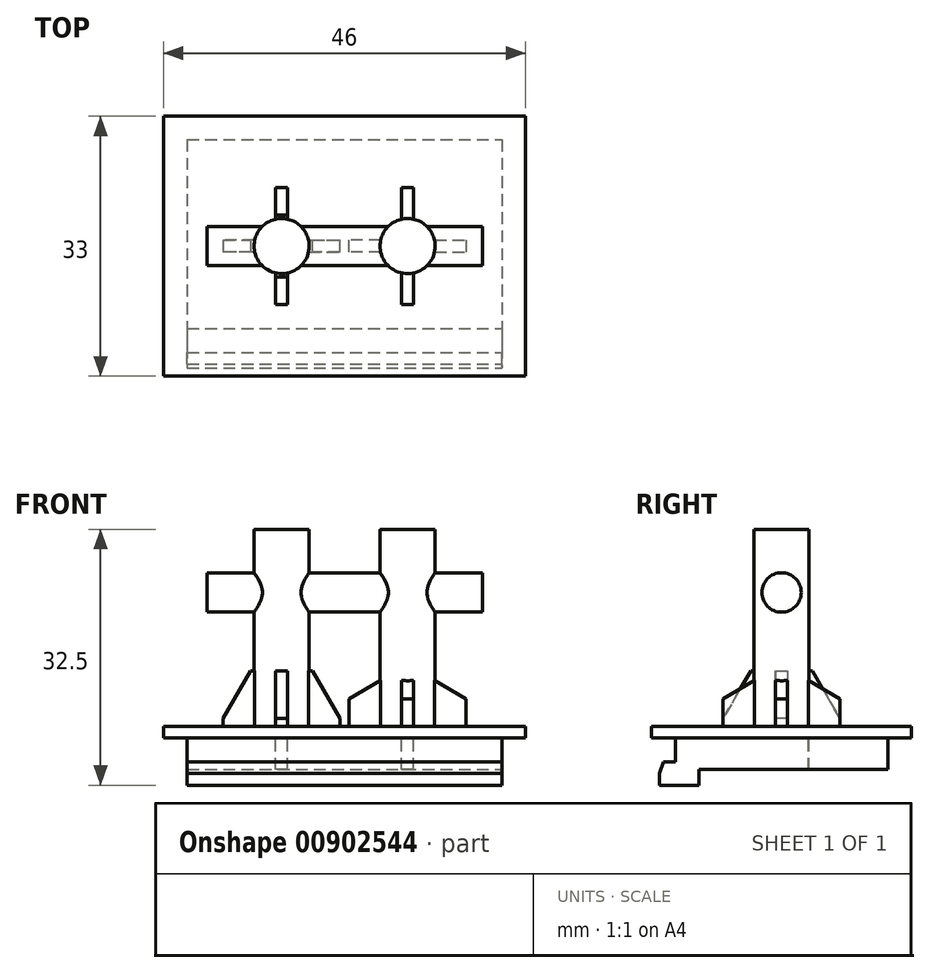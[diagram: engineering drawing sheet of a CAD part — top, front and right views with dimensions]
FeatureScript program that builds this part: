
annotation { "Feature Type Name" : "Feature", "Feature Type Description" : "" }
export const myFeature = defineFeature(function(context is Context, id is Id, definition is map)
    precondition{}
    {
        {
            var Q0;
            Q0=qCreatedBy(makeId("Top.planeOp"),FACE);
            var sketch = newSketch(context, id + "F0", { "sketchPlane" : qUnion([Q0])});
            skLineSegment(sketch, "E0.bottom", {"start": v(-20, 13.5) * mm, "end": v(20, 13.5) * mm});
            skLineSegment(sketch, "E0.top", {"start": v(-20, -13.5) * mm, "end": v(20, -13.5) * mm});
            skLineSegment(sketch, "E0.left", {"start": v(-20, 13.5) * mm, "end": v(-20, -13.5) * mm});
            skLineSegment(sketch, "E0.right", {"start": v(20, 13.5) * mm, "end": v(20, -13.5) * mm});
            skPoint(sketch, "E0.middle", {"position": v(0, 0) * mm});
            skLineSegment(sketch, "E1.bottom", {"start": v(-23, 16.5) * mm, "end": v(23, 16.5) * mm});
            skLineSegment(sketch, "E1.top", {"start": v(-23, -16.5) * mm, "end": v(23, -16.5) * mm});
            skLineSegment(sketch, "E1.left", {"start": v(-23, 16.5) * mm, "end": v(-23, -16.5) * mm});
            skLineSegment(sketch, "E1.right", {"start": v(23, 16.5) * mm, "end": v(23, -16.5) * mm});
            skLineSegment(sketch, "E2", {"start": v(0, 0) * mm, "end": v(-8, 0) * mm});
            skLineSegment(sketch, "E3", {"start": v(0, 0) * mm, "end": v(8, 0) * mm});
            skCircle(sketch, "E4", {"center": v(-8, 0) * mm, "radius": 3.5 * mm});
            skCircle(sketch, "E5", {"center": v(8, 0) * mm, "radius": 3.5 * mm});
            skLineSegment(sketch, "E6.bottom", {"start": v(-7.25, 3.42) * mm, "end": v(-8.75, 3.42) * mm});
            skLineSegment(sketch, "E6.top", {"start": v(-7.25, 7.42) * mm, "end": v(-8.75, 7.42) * mm});
            skLineSegment(sketch, "E6.left", {"start": v(-7.25, 3.42) * mm, "end": v(-7.25, 7.42) * mm});
            skLineSegment(sketch, "E6.right", {"start": v(-8.75, 3.42) * mm, "end": v(-8.75, 7.42) * mm});
            skPoint(sketch, "E6.middle", {"position": v(-8, 5.42) * mm});
            skLineSegment(sketch, "E7.bottom", {"start": v(7.25, 3.42) * mm, "end": v(8.75, 3.42) * mm});
            skLineSegment(sketch, "E7.top", {"start": v(7.25, 7.42) * mm, "end": v(8.75, 7.42) * mm});
            skLineSegment(sketch, "E7.left", {"start": v(7.25, 3.42) * mm, "end": v(7.25, 7.42) * mm});
            skLineSegment(sketch, "E7.right", {"start": v(8.75, 3.42) * mm, "end": v(8.75, 7.42) * mm});
            skPoint(sketch, "E7.middle", {"position": v(8, 5.42) * mm});
            skLineSegment(sketch, "E8.1.0", {"start": v(-11.42, -0.75) * mm, "end": v(-15.42, -0.75) * mm});
            skLineSegment(sketch, "E8.1.1", {"start": v(-15.42, 0.75) * mm, "end": v(-15.42, -0.75) * mm});
            skLineSegment(sketch, "E8.1.2", {"start": v(-11.42, 0.75) * mm, "end": v(-15.42, 0.75) * mm});
            skLineSegment(sketch, "E8.2.0", {"start": v(-7.25, -3.42) * mm, "end": v(-7.25, -7.42) * mm});
            skLineSegment(sketch, "E8.2.1", {"start": v(-8.75, -7.42) * mm, "end": v(-7.25, -7.42) * mm});
            skLineSegment(sketch, "E8.2.2", {"start": v(-8.75, -3.42) * mm, "end": v(-8.75, -7.42) * mm});
            skLineSegment(sketch, "E8.3.0", {"start": v(-4.58, 0.75) * mm, "end": v(-0.58, 0.75) * mm});
            skLineSegment(sketch, "E8.3.1", {"start": v(-0.58, -0.75) * mm, "end": v(-0.58, 0.75) * mm});
            skLineSegment(sketch, "E8.3.2", {"start": v(-4.58, -0.75) * mm, "end": v(-0.58, -0.75) * mm});
            skLineSegment(sketch, "E9.1.0", {"start": v(0.58, -0.75) * mm, "end": v(0.58, 0.75) * mm});
            skLineSegment(sketch, "E9.1.1", {"start": v(4.58, 0.75) * mm, "end": v(0.58, 0.75) * mm});
            skLineSegment(sketch, "E9.1.2", {"start": v(4.58, -0.75) * mm, "end": v(0.58, -0.75) * mm});
            skLineSegment(sketch, "E9.2.0", {"start": v(8.75, -7.42) * mm, "end": v(7.25, -7.42) * mm});
            skLineSegment(sketch, "E9.2.1", {"start": v(7.25, -3.42) * mm, "end": v(7.25, -7.42) * mm});
            skLineSegment(sketch, "E9.2.2", {"start": v(8.75, -3.42) * mm, "end": v(8.75, -7.42) * mm});
            skLineSegment(sketch, "E9.3.0", {"start": v(15.42, 0.75) * mm, "end": v(15.42, -0.75) * mm});
            skLineSegment(sketch, "E9.3.1", {"start": v(11.42, -0.75) * mm, "end": v(15.42, -0.75) * mm});
            skLineSegment(sketch, "E9.3.2", {"start": v(11.42, 0.75) * mm, "end": v(15.42, 0.75) * mm});
            skSolve(sketch);
        }
        {
            var Q0;
            Q0 = qSketchRegion(id + "F0", true);
            var Q1;
            Q1=makeQuery(id+"F0.imprint","IMPRINT",FACE,{"disambiguationData":[TD([[makeQuery(id+"F0.imprint","IMPRINT",EDGE,{"derivedFrom":sQuery(id+"F0.wireOp",EDGE,"E0.bottom")}),-1.0]])]});
            var Q2;
            Q2=makeQuery(id+"F0.imprint","IMPRINT",FACE,{"disambiguationData":[TD([[makeQuery(id+"F0.imprint","IMPRINT",EDGE,{"derivedFrom":sQuery(id+"F0.wireOp",EDGE,"E4")}),1.0]])]});
            var Q3;
            Q3=makeQuery(id+"F0.imprint","IMPRINT",FACE,{"disambiguationData":[TD([[makeQuery(id+"F0.imprint","IMPRINT",EDGE,{"derivedFrom":sQuery(id+"F0.wireOp",EDGE,"E5")}),1.0]])]});
            var Q4;
            {var subQ0=sQuery(id+"F0.wireOp",EDGE,"E8.2.0");Q4=makeQuery(id+"F0.imprint","IMPRINT",FACE,{"disambiguationData":[TD([[makeQuery(id+"F0.imprint","IMPRINT",EDGE,{"derivedFrom":subQ0}),-1.0]])]});}
            var Q5;
            Q5=makeQuery(id+"F0.imprint","IMPRINT",FACE,{"disambiguationData":[TD([[makeQuery(id+"F0.imprint","IMPRINT",EDGE,{"derivedFrom":sQuery(id+"F0.wireOp",EDGE,"E6.top")}),1.0]])]});
            var Q6;
            {var subQ0=sQuery(id+"F0.wireOp",EDGE,"E8.1.0");Q6=makeQuery(id+"F0.imprint","IMPRINT",FACE,{"disambiguationData":[TD([[makeQuery(id+"F0.imprint","IMPRINT",EDGE,{"derivedFrom":subQ0}),-1.0]])]});}
            var Q7;
            {var subQ5=sQuery(id+"F0.wireOp",EDGE,"E8.3.0");Q7=makeQuery(id+"F0.imprint","IMPRINT",FACE,{"disambiguationData":[TD([[makeQuery(id+"F0.imprint","IMPRINT",EDGE,{"derivedFrom":subQ5}),-1.0]])]});}
            var Q8;
            {var subQ5=sQuery(id+"F0.wireOp",EDGE,"E8.3.2");Q8=makeQuery(id+"F0.imprint","IMPRINT",FACE,{"disambiguationData":[TD([[makeQuery(id+"F0.imprint","IMPRINT",EDGE,{"derivedFrom":subQ5}),1.0]])]});}
            var Q9;
            {var subQ5=sQuery(id+"F0.wireOp",EDGE,"E9.1.2");Q9=makeQuery(id+"F0.imprint","IMPRINT",FACE,{"disambiguationData":[TD([[makeQuery(id+"F0.imprint","IMPRINT",EDGE,{"derivedFrom":subQ5}),-1.0]])]});}
            var Q10;
            {var subQ5=sQuery(id+"F0.wireOp",EDGE,"E9.1.1");Q10=makeQuery(id+"F0.imprint","IMPRINT",FACE,{"disambiguationData":[TD([[makeQuery(id+"F0.imprint","IMPRINT",EDGE,{"derivedFrom":subQ5}),1.0]])]});}
            var Q11;
            Q11=makeQuery(id+"F0.imprint","IMPRINT",FACE,{"disambiguationData":[TD([[makeQuery(id+"F0.imprint","IMPRINT",EDGE,{"derivedFrom":sQuery(id+"F0.wireOp",EDGE,"E7.top")}),-1.0]])]});
            var Q12;
            Q12=makeQuery(id+"F0.imprint","IMPRINT",FACE,{"disambiguationData":[TD([[makeQuery(id+"F0.imprint","IMPRINT",EDGE,{"derivedFrom":sQuery(id+"F0.wireOp",EDGE,"E9.3.0")}),-1.0]])]});
            var Q13;
            Q13=makeQuery(id+"F0.imprint","IMPRINT",FACE,{"disambiguationData":[TD([[makeQuery(id+"F0.imprint","IMPRINT",EDGE,{"derivedFrom":sQuery(id+"F0.wireOp",EDGE,"E9.2.0")}),-1.0]])]});
            var Q14;
            {var subQ0=sQuery(id+"F0.wireOp",EDGE,"E7.bottom");Q14=makeQuery(id+"F0.imprint","IMPRINT",FACE,{"disambiguationData":[TD([[makeQuery(id+"F0.imprint","IMPRINT",EDGE,{"derivedFrom":subQ0}),1.0]])]});}
            var Q15;
            {var subQ0=sQuery(id+"F0.wireOp",EDGE,"E6.bottom");Q15=makeQuery(id+"F0.imprint","IMPRINT",FACE,{"disambiguationData":[TD([[makeQuery(id+"F0.imprint","IMPRINT",EDGE,{"derivedFrom":subQ0}),-1.0]])]});}
            extrude(context, id + "F1", {"entities" : qUnion([Q0, Q1, Q2, Q3, Q4, Q5, Q6, Q7, Q8, Q9, Q10, Q11, Q12, Q13, Q14, Q15]), "oppositeDirection" : true, "depth" : 1.5 * mm, "offsetDistance" : 25 * mm});
        }
        {
            var Q0;
            {var subQ0=sQuery(id+"F0.wireOp",EDGE,"E8.2.0");Q0=makeQuery(id+"F0.imprint","IMPRINT",FACE,{"disambiguationData":[TD([[makeQuery(id+"F0.imprint","IMPRINT",EDGE,{"derivedFrom":subQ0}),-1.0]])]});}
            var Q1;
            {var subQ0=sQuery(id+"F0.wireOp",EDGE,"E8.1.0");Q1=makeQuery(id+"F0.imprint","IMPRINT",FACE,{"disambiguationData":[TD([[makeQuery(id+"F0.imprint","IMPRINT",EDGE,{"derivedFrom":subQ0}),-1.0]])]});}
            var Q2;
            Q2=makeQuery(id+"F0.imprint","IMPRINT",FACE,{"disambiguationData":[TD([[makeQuery(id+"F0.imprint","IMPRINT",EDGE,{"derivedFrom":sQuery(id+"F0.wireOp",EDGE,"E6.top")}),1.0]])]});
            var Q3;
            {var subQ5=sQuery(id+"F0.wireOp",EDGE,"E9.1.2");Q3=makeQuery(id+"F0.imprint","IMPRINT",FACE,{"disambiguationData":[TD([[makeQuery(id+"F0.imprint","IMPRINT",EDGE,{"derivedFrom":subQ5}),-1.0]])]});}
            var Q4;
            {var subQ5=sQuery(id+"F0.wireOp",EDGE,"E9.1.1");Q4=makeQuery(id+"F0.imprint","IMPRINT",FACE,{"disambiguationData":[TD([[makeQuery(id+"F0.imprint","IMPRINT",EDGE,{"derivedFrom":subQ5}),1.0]])]});}
            var Q5;
            {var subQ5=sQuery(id+"F0.wireOp",EDGE,"E8.3.2");Q5=makeQuery(id+"F0.imprint","IMPRINT",FACE,{"disambiguationData":[TD([[makeQuery(id+"F0.imprint","IMPRINT",EDGE,{"derivedFrom":subQ5}),1.0]])]});}
            var Q6;
            {var subQ5=sQuery(id+"F0.wireOp",EDGE,"E8.3.0");Q6=makeQuery(id+"F0.imprint","IMPRINT",FACE,{"disambiguationData":[TD([[makeQuery(id+"F0.imprint","IMPRINT",EDGE,{"derivedFrom":subQ5}),-1.0]])]});}
            var Q7;
            Q7=makeQuery(id+"F0.imprint","IMPRINT",FACE,{"disambiguationData":[TD([[makeQuery(id+"F0.imprint","IMPRINT",EDGE,{"derivedFrom":sQuery(id+"F0.wireOp",EDGE,"E7.top")}),-1.0]])]});
            var Q8;
            Q8=makeQuery(id+"F0.imprint","IMPRINT",FACE,{"disambiguationData":[TD([[makeQuery(id+"F0.imprint","IMPRINT",EDGE,{"derivedFrom":sQuery(id+"F0.wireOp",EDGE,"E9.3.0")}),-1.0]])]});
            var Q9;
            Q9=makeQuery(id+"F0.imprint","IMPRINT",FACE,{"disambiguationData":[TD([[makeQuery(id+"F0.imprint","IMPRINT",EDGE,{"derivedFrom":sQuery(id+"F0.wireOp",EDGE,"E9.2.0")}),-1.0]])]});
            var Q10;
            Q10=makeQuery(id+"F0.imprint","IMPRINT",FACE,{"disambiguationData":[TD([[makeQuery(id+"F0.imprint","IMPRINT",EDGE,{"derivedFrom":sQuery(id+"F0.wireOp",EDGE,"E0.bottom")}),-1.0]])]});
            var Q11;
            {var subQ3=sQuery(id+"F0.wireOp",EDGE,"E6.bottom");Q11=makeQuery(id+"F0.imprint","IMPRINT",FACE,{"disambiguationData":[TD([[makeQuery(id+"F0.imprint","IMPRINT",EDGE,{"derivedFrom":subQ3}),1.0]])]});}
            var Q12;
            {var subQ4=sQuery(id+"F0.wireOp",EDGE,"E7.bottom");Q12=makeQuery(id+"F0.imprint","IMPRINT",FACE,{"disambiguationData":[TD([[makeQuery(id+"F0.imprint","IMPRINT",EDGE,{"derivedFrom":subQ4}),-1.0]])]});}
            extrude(context, id + "F2", {"entities" : qUnion([Q0, Q1, Q2, Q3, Q4, Q5, Q6, Q7, Q8, Q9, Q10, Q11, Q12]), "operationType" : NewBodyOperationType.ADD, "oppositeDirection" : true, "depth" : 5.5 * mm, "offsetDistance" : 25 * mm});
        }
        {
            var Q0;
            Q0=makeQuery(id+"F0.imprint","IMPRINT",FACE,{"disambiguationData":[TD([[makeQuery(id+"F0.imprint","IMPRINT",EDGE,{"derivedFrom":sQuery(id+"F0.wireOp",EDGE,"E4")}),1.0]])]});
            var Q1;
            Q1=makeQuery(id+"F0.imprint","IMPRINT",FACE,{"disambiguationData":[TD([[makeQuery(id+"F0.imprint","IMPRINT",EDGE,{"derivedFrom":sQuery(id+"F0.wireOp",EDGE,"E5")}),1.0]])]});
            var Q2;
            {var subQ0=sQuery(id+"F0.wireOp",EDGE,"E6.bottom");Q2=makeQuery(id+"F0.imprint","IMPRINT",FACE,{"disambiguationData":[TD([[makeQuery(id+"F0.imprint","IMPRINT",EDGE,{"derivedFrom":subQ0}),-1.0]])]});}
            var Q3;
            {var subQ0=sQuery(id+"F0.wireOp",EDGE,"E7.bottom");Q3=makeQuery(id+"F0.imprint","IMPRINT",FACE,{"disambiguationData":[TD([[makeQuery(id+"F0.imprint","IMPRINT",EDGE,{"derivedFrom":subQ0}),1.0]])]});}
            extrude(context, id + "F3", {"entities" : qUnion([Q0, Q1, Q2, Q3]), "operationType" : NewBodyOperationType.ADD, "depth" : 25 * mm, "offsetDistance" : 25 * mm});
        }
        {
            var Q0;
            Q0=qCreatedBy(makeId("Right.planeOp"),FACE);
            var sketch = newSketch(context, id + "F4", { "sketchPlane" : qUnion([Q0])});
            skCircle(sketch, "E10", {"center": v(0, 17) * mm, "radius": 2.5 * mm});
            skSolve(sketch);
        }
        {
            var Q0;
            Q0=makeQuery(id+"F4.imprint","IMPRINT",FACE,{"disambiguationData":[TD([[makeQuery(id+"F4.imprint","IMPRINT",EDGE,{"derivedFrom":sQuery(id+"F4.wireOp",EDGE,"E10")}),1.0]])]});
            extrude(context, id + "F5", {"entities" : qUnion([Q0]), "operationType" : NewBodyOperationType.ADD, "depth" : 35 * mm, "offsetDistance" : 25 * mm, "symmetric" : true});
        }
        {
            var Q0;
            Q0=makeQuery(id+"F0.imprint","IMPRINT",FACE,{"disambiguationData":[TD([[makeQuery(id+"F0.imprint","IMPRINT",EDGE,{"derivedFrom":sQuery(id+"F0.wireOp",EDGE,"E6.top")}),1.0]])]});
            var Q1;
            {var subQ0=sQuery(id+"F0.wireOp",EDGE,"E8.2.0");Q1=makeQuery(id+"F0.imprint","IMPRINT",FACE,{"disambiguationData":[TD([[makeQuery(id+"F0.imprint","IMPRINT",EDGE,{"derivedFrom":subQ0}),-1.0]])]});}
            var Q2;
            {var subQ0=sQuery(id+"F0.wireOp",EDGE,"E8.1.0");Q2=makeQuery(id+"F0.imprint","IMPRINT",FACE,{"disambiguationData":[TD([[makeQuery(id+"F0.imprint","IMPRINT",EDGE,{"derivedFrom":subQ0}),-1.0]])]});}
            var Q3;
            {var subQ5=sQuery(id+"F0.wireOp",EDGE,"E8.3.2");Q3=makeQuery(id+"F0.imprint","IMPRINT",FACE,{"disambiguationData":[TD([[makeQuery(id+"F0.imprint","IMPRINT",EDGE,{"derivedFrom":subQ5}),1.0]])]});}
            var Q4;
            {var subQ5=sQuery(id+"F0.wireOp",EDGE,"E9.1.2");Q4=makeQuery(id+"F0.imprint","IMPRINT",FACE,{"disambiguationData":[TD([[makeQuery(id+"F0.imprint","IMPRINT",EDGE,{"derivedFrom":subQ5}),-1.0]])]});}
            var Q5;
            Q5=makeQuery(id+"F0.imprint","IMPRINT",FACE,{"disambiguationData":[TD([[makeQuery(id+"F0.imprint","IMPRINT",EDGE,{"derivedFrom":sQuery(id+"F0.wireOp",EDGE,"E9.2.0")}),-1.0]])]});
            var Q6;
            Q6=makeQuery(id+"F0.imprint","IMPRINT",FACE,{"disambiguationData":[TD([[makeQuery(id+"F0.imprint","IMPRINT",EDGE,{"derivedFrom":sQuery(id+"F0.wireOp",EDGE,"E9.3.0")}),-1.0]])]});
            var Q7;
            Q7=makeQuery(id+"F0.imprint","IMPRINT",FACE,{"disambiguationData":[TD([[makeQuery(id+"F0.imprint","IMPRINT",EDGE,{"derivedFrom":sQuery(id+"F0.wireOp",EDGE,"E7.top")}),-1.0]])]});
            var Q8;
            {var subQ5=sQuery(id+"F0.wireOp",EDGE,"E8.3.0");Q8=makeQuery(id+"F0.imprint","IMPRINT",FACE,{"disambiguationData":[TD([[makeQuery(id+"F0.imprint","IMPRINT",EDGE,{"derivedFrom":subQ5}),-1.0]])]});}
            var Q9;
            {var subQ5=sQuery(id+"F0.wireOp",EDGE,"E9.1.1");Q9=makeQuery(id+"F0.imprint","IMPRINT",FACE,{"disambiguationData":[TD([[makeQuery(id+"F0.imprint","IMPRINT",EDGE,{"derivedFrom":subQ5}),1.0]])]});}
            extrude(context, id + "F6", {"entities" : qUnion([Q0, Q1, Q2, Q3, Q4, Q5, Q6, Q7, Q8, Q9]), "operationType" : NewBodyOperationType.ADD, "depth" : 7 * mm, "offsetDistance" : 25 * mm});
        }
        {
            var Q0;
            Q0=makeQuery(id+"F6.opExtrude","CAP_EDGE",EDGE,{"disambiguationData":[OSD([sQuery(id+"F0.wireOp",EDGE,"E8.2.1")])],"isStart":false});
            var Q1;
            Q1=makeQuery(id+"F6.opExtrude","CAP_EDGE",EDGE,{"disambiguationData":[OSD([sQuery(id+"F0.wireOp",EDGE,"E8.3.1")])],"isStart":false});
            var Q2;
            Q2=makeQuery(id+"F6.opExtrude","CAP_EDGE",EDGE,{"disambiguationData":[OSD([sQuery(id+"F0.wireOp",EDGE,"E6.top")])],"isStart":false});
            var Q3;
            Q3=makeQuery(id+"F6.opExtrude","CAP_EDGE",EDGE,{"disambiguationData":[OSD([sQuery(id+"F0.wireOp",EDGE,"E8.1.1")])],"isStart":false});
            chamfer(context, id + "F7", {"entities" : qUnion([Q0, Q1, Q2, Q3]), "chamferType" : ChamferType.TWO_OFFSETS, "width1" : 3.5 * mm, "oppositeDirection" : false, "width2" : 6 * mm, "tangentPropagation" : true});
        }
        {
            var Q0;
            Q0=makeQuery(id+"F6.opExtrude","CAP_EDGE",EDGE,{"disambiguationData":[OSD([sQuery(id+"F0.wireOp",EDGE,"E9.1.0")])],"isStart":false});
            var Q1;
            Q1=makeQuery(id+"F6.opExtrude","CAP_EDGE",EDGE,{"disambiguationData":[OSD([sQuery(id+"F0.wireOp",EDGE,"E9.2.0")])],"isStart":false});
            var Q2;
            Q2=makeQuery(id+"F6.opExtrude","CAP_EDGE",EDGE,{"disambiguationData":[OSD([sQuery(id+"F0.wireOp",EDGE,"E9.3.0")])],"isStart":false});
            var Q3;
            Q3=makeQuery(id+"F6.opExtrude","CAP_EDGE",EDGE,{"disambiguationData":[OSD([sQuery(id+"F0.wireOp",EDGE,"E7.top")])],"isStart":false});
            chamfer(context, id + "F8", {"entities" : qUnion([Q0, Q1, Q2, Q3]), "chamferType" : ChamferType.TWO_OFFSETS, "width1" : 6 * mm, "oppositeDirection" : false, "width2" : 3.5 * mm, "tangentPropagation" : true});
        }
        {
            var Q0;
            Q0=makeQuery(id+"F2.opExtrude","CAP_FACE",FACE,{"disambiguationData":[OSD([sQuery(id+"F0.wireOp",EDGE,"E0.bottom"),sQuery(id+"F0.wireOp",EDGE,"E0.top"),sQuery(id+"F0.wireOp",EDGE,"E0.left"),sQuery(id+"F0.wireOp",EDGE,"E0.right"),sQuery(id+"F0.wireOp",EDGE,"E4"),sQuery(id+"F0.wireOp",EDGE,"E5"),sQuery(id+"F0.wireOp",EDGE,"E6.bottom"),sQuery(id+"F0.wireOp",EDGE,"E7.bottom")])],"isStart":false});
            var sketch = newSketch(context, id + "F9", { "sketchPlane" : qUnion([Q0])});
            skLineSegment(sketch, "E11.bottom", {"start": v(-20, 13.5) * mm, "end": v(20, 13.5) * mm});
            skLineSegment(sketch, "E11.top", {"start": v(-20, 10.5) * mm, "end": v(20, 10.5) * mm});
            skLineSegment(sketch, "E11.left", {"start": v(-20, 13.5) * mm, "end": v(-20, 10.5) * mm});
            skLineSegment(sketch, "E11.right", {"start": v(20, 13.5) * mm, "end": v(20, 10.5) * mm});
            skSolve(sketch);
        }
        {
            var Q0;
            Q0=makeQuery(id+"F9.imprint","IMPRINT",FACE,{"disambiguationData":[TD([[makeQuery(id+"F9.imprint","IMPRINT",EDGE,{"derivedFrom":sQuery(id+"F9.wireOp",EDGE,"E11.bottom")}),-1.0]])]});
            extrude(context, id + "F10", {"entities" : qUnion([Q0]), "operationType" : NewBodyOperationType.ADD, "depth" : 2 * mm, "offsetDistance" : 25 * mm});
        }
        {
            var Q0;
            Q0=makeQuery(id+"F10.boolean.opBoolean","MERGE",FACE,{"derivedFrom":[makeQuery(id+"F2.opExtrude","SWEPT_FACE",FACE,{"disambiguationData":[OSD([sQuery(id+"F0.wireOp",EDGE,"E0.top")])]}),makeQuery(id+"F10.opExtrude","SWEPT_FACE",FACE,{"disambiguationData":[OSD([sQuery(id+"F9.wireOp",EDGE,"E11.bottom")])]})]});
            var sketch = newSketch(context, id + "F11", { "sketchPlane" : qUnion([Q0])});
            skLineSegment(sketch, "E12.bottom", {"start": v(-20, -7.5) * mm, "end": v(20, -7.5) * mm});
            skLineSegment(sketch, "E12.top", {"start": v(-20, -4.5) * mm, "end": v(20, -4.5) * mm});
            skLineSegment(sketch, "E12.left", {"start": v(-20, -7.5) * mm, "end": v(-20, -4.5) * mm});
            skLineSegment(sketch, "E12.right", {"start": v(20, -7.5) * mm, "end": v(20, -4.5) * mm});
            skSolve(sketch);
        }
        {
            var Q0;
            Q0=makeQuery(id+"F11.imprint","IMPRINT",FACE,{"disambiguationData":[TD([[makeQuery(id+"F11.imprint","IMPRINT",EDGE,{"derivedFrom":sQuery(id+"F11.wireOp",EDGE,"E12.bottom")}),1.0]])]});
            extrude(context, id + "F12", {"entities" : qUnion([Q0]), "operationType" : NewBodyOperationType.ADD, "depth" : 2 * mm, "offsetDistance" : 25 * mm});
        }
        {
            var Q0;
            Q0=makeQuery(id+"F12.opExtrude","CAP_EDGE",EDGE,{"disambiguationData":[OSD([sQuery(id+"F11.wireOp",EDGE,"E12.top")])],"isStart":false});
            chamfer(context, id + "F13", {"entities" : qUnion([Q0]), "chamferType" : ChamferType.TWO_OFFSETS, "width1" : 1.5 * mm, "oppositeDirection" : false, "width2" : 0.5 * mm, "tangentPropagation" : true});
        }
    });
